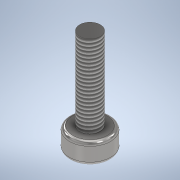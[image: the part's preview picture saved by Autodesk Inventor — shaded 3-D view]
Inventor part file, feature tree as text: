
AUTODESK INVENTOR PART (.ipt)
format: ipt  version: 2021 (Build 250183000, 183)  size: 129,024 bytes
history: native  units: mm
features: extrude x2, sketch x2, fillet x1, thread x1
ambient origin geometry x8: Origin, YZ Plane, XZ Plane, XY Plane, X Axis, Y Axis, Z Axis, Center Point
bodies: Solid1 (feature_tree)
feature tree (6):
  extrude  "Extrusion1"  Depth=3.0mm TaperAngle=0.0deg
  extrude  "Extrusion2"  Depth=12.0mm TaperAngle=0.0deg
  fillet  "Fillet1"  Radius=12.0mm
  thread  "Thread1"  [1 undecoded]
  sketch  "Sketch1"  dims[d0=6.0mm d1=3.0mm d2=0.0mm]
  sketch  "Sketch2"  dims[d3=3.0mm d4=12.0mm d5=0.0mm d6=12.0mm d7=0.0mm d8=0.5mm]
note: 1 required parameter value undecoded (feature->parameter linkage not recoverable at this tier; creation-order binding heuristic only, values carry confidence <= 0.55)
